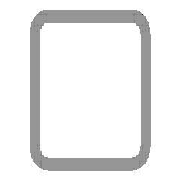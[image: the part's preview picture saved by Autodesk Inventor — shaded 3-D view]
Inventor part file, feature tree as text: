
AUTODESK INVENTOR PART (.ipt)
format: ipt  version: 2022 (Build 260153000, 153)  size: 153,088 bytes
history: native  units: mm (DEFAULTED — no unit token found)
features: other x4, plane x3, sketch x3, split x2
ambient origin geometry x8: Origin, YZ Plane, XZ Plane, XY Plane, X Axis, Y Axis, Z Axis, Center Point
bodies: Solid1 (feature_tree), Body (feature_tree)
feature tree (12):
  parser-record x1  (decoder bookkeeping rows leaked as tree rows — omitted from the tree; the rows remain in map.json)
  other  "Driven Length"
  other  "Start Plane"
  other  "End Plane"
  plane  "Work Plane4"
  split  "Split1"
  plane  "Work Plane5"
  split  "Split2"
  sketch  "Sketch"  dims[d7=4.0mm d9=40.0mm d11=40.0mm d12=2.0mm d13=-20.0mm d14=305.182521mm d15=20.0mm d16=20.0mm d17=90.0deg d18=325.182521mm]
  sketch  "Sketch3"  dims[d3=325.182521mm]
  plane  "Work Plane3"
  sketch  "Sketch4"  dims[d4=0.0mm]
